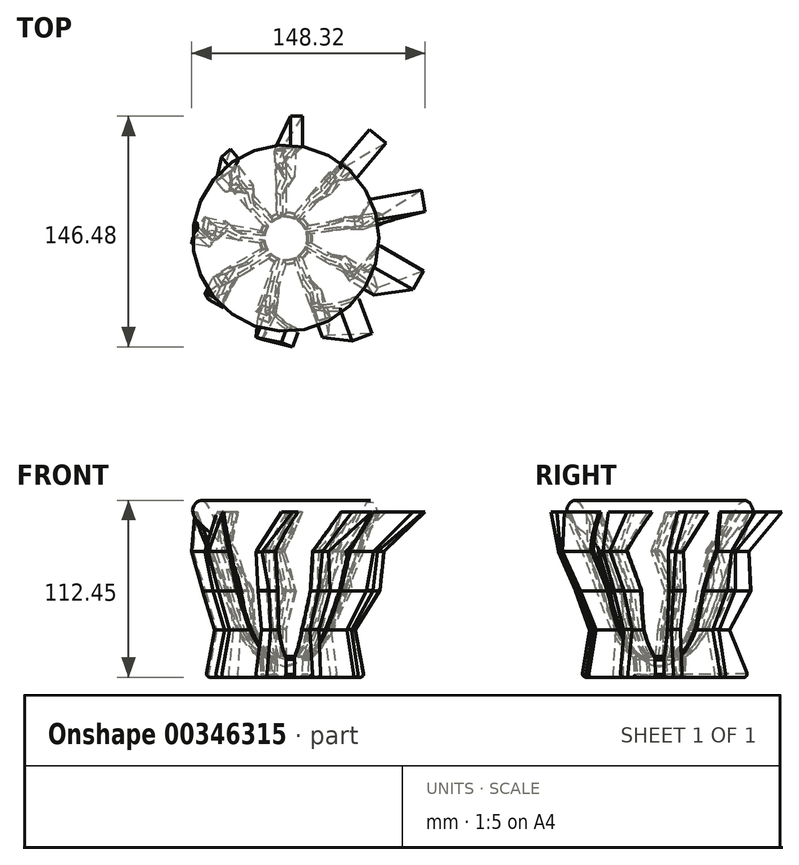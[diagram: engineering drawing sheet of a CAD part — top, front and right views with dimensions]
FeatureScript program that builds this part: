
annotation { "Feature Type Name" : "Feature", "Feature Type Description" : "" }
export const myFeature = defineFeature(function(context is Context, id is Id, definition is map)
    precondition{}
    {
        {
            var Q0;
            Q0=qCreatedBy(makeId("Top.planeOp"),FACE);
            var sketch = newSketch(context, id + "F0", { "sketchPlane" : qUnion([Q0])});
            skLineSegment(sketch, "E0", {"start": v(-7.56, 56.38) * mm, "end": v(0, 56.38) * mm});
            skLineSegment(sketch, "E1", {"start": v(0, 56.38) * mm, "end": v(0, 16) * mm});
            skLineSegment(sketch, "E2.1.1", {"start": v(-36.67, 35.22) * mm, "end": v(-30.87, 40.08) * mm});
            skLineSegment(sketch, "E2.1.2", {"start": v(-30.87, 40.08) * mm, "end": v(-8.58, 13.5) * mm});
            skLineSegment(sketch, "E2.2.1", {"start": v(-50.73, 3.4) * mm, "end": v(-49.41, 10.86) * mm});
            skLineSegment(sketch, "E2.2.2", {"start": v(-49.41, 10.86) * mm, "end": v(-15.25, 4.83) * mm});
            skLineSegment(sketch, "E2.3.1", {"start": v(-41.05, -30) * mm, "end": v(-44.83, -23.44) * mm});
            skLineSegment(sketch, "E2.3.2", {"start": v(-44.83, -23.44) * mm, "end": v(-14.8, -6.1) * mm});
            skLineSegment(sketch, "E2.4.1", {"start": v(-12.17, -49.36) * mm, "end": v(-19.27, -46.78) * mm});
            skLineSegment(sketch, "E2.4.2", {"start": v(-19.27, -46.78) * mm, "end": v(-7.4, -14.18) * mm});
            skLineSegment(sketch, "E2.5.1", {"start": v(22.28, -45.29) * mm, "end": v(17.16, -47.15) * mm});
            skLineSegment(sketch, "E2.5.2", {"start": v(17.16, -47.15) * mm, "end": v(5.47, -15.04) * mm});
            skLineSegment(sketch, "E2.6.1", {"start": v(46.18, -20.37) * mm, "end": v(43.45, -25.09) * mm});
            skLineSegment(sketch, "E2.6.2", {"start": v(43.45, -25.09) * mm, "end": v(13.86, -8) * mm});
            skLineSegment(sketch, "E2.7.1", {"start": v(48.83, 14.15) * mm, "end": v(49.78, 8.78) * mm});
            skLineSegment(sketch, "E2.7.2", {"start": v(49.78, 8.78) * mm, "end": v(15.76, 2.78) * mm});
            skLineSegment(sketch, "E2.8.1", {"start": v(28.32, 42.23) * mm, "end": v(32.5, 38.72) * mm});
            skLineSegment(sketch, "E2.8.2", {"start": v(32.5, 38.72) * mm, "end": v(10.28, 12.26) * mm});
            skPoint(sketch, "E2.center", {"position": v(0, 0) * mm});
            skArc(sketch, "E3", {"start": v(-13.84, 8.02) * mm, "mid": v(-14.64, 6.47) * mm, "end": v(-15.25, 4.83) * mm});
            skArc(sketch, "E4.trimOffspring", {"start": v(-5.45, 15.04) * mm, "mid": v(-7.06, 14.36) * mm, "end": v(-8.58, 13.5) * mm});
            skArc(sketch, "E5.trimOffspring", {"start": v(5.5, 15.03) * mm, "mid": v(2.79, 15.75) * mm, "end": v(0, 16) * mm});
            skLineSegment(sketch, "E6.trimOffspring", {"start": v(-5.45, 15.04) * mm, "end": v(-7.56, 56.38) * mm});
            skLineSegment(sketch, "E7.trimOffspring", {"start": v(15.75, -2.8) * mm, "end": v(46.18, -20.37) * mm});
            skLineSegment(sketch, "E8.trimOffspring", {"start": v(13.87, 7.98) * mm, "end": v(48.83, 14.15) * mm});
            skLineSegment(sketch, "E9.trimOffspring", {"start": v(5.5, 15.03) * mm, "end": v(28.32, 42.23) * mm});
            skLineSegment(sketch, "E10.trimOffspring", {"start": v(-13.84, 8.02) * mm, "end": v(-36.67, 35.22) * mm});
            skLineSegment(sketch, "E11.trimOffspring", {"start": v(-15.76, -2.76) * mm, "end": v(-50.73, 3.4) * mm});
            skArc(sketch, "E12.trimOffspring", {"start": v(-15.76, -2.76) * mm, "mid": v(-15.37, -4.45) * mm, "end": v(-14.8, -6.1) * mm});
            skArc(sketch, "E13.trimOffspring", {"start": v(-10.3, -12.24) * mm, "mid": v(-8.9, -13.3) * mm, "end": v(-7.4, -14.18) * mm});
            skLineSegment(sketch, "E14.trimOffspring", {"start": v(-10.3, -12.24) * mm, "end": v(-41.05, -30) * mm});
            skArc(sketch, "E15.trimOffspring", {"start": v(-0.02, -16) * mm, "mid": v(2.77, -15.76) * mm, "end": v(5.47, -15.04) * mm});
            skLineSegment(sketch, "E16.trimOffspring", {"start": v(-0.02, -16) * mm, "end": v(-12.17, -49.36) * mm});
            skLineSegment(sketch, "E17.trimOffspring", {"start": v(10.27, -12.27) * mm, "end": v(22.28, -45.29) * mm});
            skArc(sketch, "E18.trimOffspring", {"start": v(13.87, 7.98) * mm, "mid": v(12.26, 10.28) * mm, "end": v(10.28, 12.26) * mm});
            skArc(sketch, "E19.trimOffspring", {"start": v(15.75, -2.8) * mm, "mid": v(16, -0.01) * mm, "end": v(15.76, 2.78) * mm});
            skArc(sketch, "E20.trimOffspring", {"start": v(10.27, -12.27) * mm, "mid": v(12.25, -10.3) * mm, "end": v(13.86, -8) * mm});
            skSolve(sketch);
        }
        {
            var Q0;
            Q0=qCreatedBy(makeId("Top.planeOp"),FACE);
            cPlane(context, id + "F1", {"entities" : qUnion([Q0]), "cplaneType" : CPlaneType.OFFSET, "offset" : 30 * mm, "width" : 150 * mm, "height" : 150 * mm});
        }
        {
            var Q0;
            Q0=qCreatedBy(id+"F1.planeOp",FACE);
            cPlane(context, id + "F2", {"entities" : qUnion([Q0]), "cplaneType" : CPlaneType.OFFSET, "offset" : 25 * mm, "width" : 150 * mm, "height" : 150 * mm});
        }
        {
            var Q0;
            Q0=qCreatedBy(id+"F1.planeOp",FACE);
            var sketch = newSketch(context, id + "F3", { "sketchPlane" : qUnion([Q0])});
            skLineSegment(sketch, "E21", {"start": v(-6, 44.23) * mm, "end": v(0, 44.23) * mm});
            skLineSegment(sketch, "E22", {"start": v(0, 44.23) * mm, "end": v(0, 17.12) * mm});
            skLineSegment(sketch, "E23.1.1", {"start": v(-33.34, 29.91) * mm, "end": v(-28.74, 33.77) * mm});
            skLineSegment(sketch, "E23.1.2", {"start": v(-28.74, 33.77) * mm, "end": v(-11.31, 13) * mm});
            skLineSegment(sketch, "E23.2.1", {"start": v(-45.08, 1.36) * mm, "end": v(-44.04, 7.27) * mm});
            skLineSegment(sketch, "E23.2.2", {"start": v(-44.04, 7.27) * mm, "end": v(-17.34, 2.56) * mm});
            skLineSegment(sketch, "E23.3.1", {"start": v(-35.73, -28.05) * mm, "end": v(-38.73, -22.86) * mm});
            skLineSegment(sketch, "E23.3.2", {"start": v(-38.73, -22.86) * mm, "end": v(-15.24, -9.3) * mm});
            skLineSegment(sketch, "E23.4.1", {"start": v(-9.65, -44.58) * mm, "end": v(-15.29, -42.52) * mm});
            skLineSegment(sketch, "E23.4.2", {"start": v(-15.29, -42.52) * mm, "end": v(-6.02, -17.04) * mm});
            skLineSegment(sketch, "E23.5.1", {"start": v(20.94, -40.47) * mm, "end": v(15.3, -42.52) * mm});
            skLineSegment(sketch, "E23.5.2", {"start": v(15.3, -42.52) * mm, "end": v(6.03, -17.04) * mm});
            skLineSegment(sketch, "E23.6.1", {"start": v(41.74, -17.66) * mm, "end": v(38.74, -22.86) * mm});
            skLineSegment(sketch, "E23.6.2", {"start": v(38.74, -22.86) * mm, "end": v(15.26, -9.3) * mm});
            skLineSegment(sketch, "E23.7.1", {"start": v(43.01, 13.18) * mm, "end": v(44.06, 7.27) * mm});
            skLineSegment(sketch, "E23.7.2", {"start": v(44.06, 7.27) * mm, "end": v(17.35, 2.56) * mm});
            skLineSegment(sketch, "E23.8.1", {"start": v(24.16, 37.63) * mm, "end": v(28.76, 33.77) * mm});
            skLineSegment(sketch, "E23.8.2", {"start": v(28.76, 33.77) * mm, "end": v(11.33, 13) * mm});
            skPoint(sketch, "E23.center", {"position": v(0, -0.5) * mm});
            skArc(sketch, "E24", {"start": v(-15.23, 8.33) * mm, "mid": v(-16.54, 5.54) * mm, "end": v(-17.34, 2.56) * mm});
            skArc(sketch, "E25.trimOffspring", {"start": v(-6, 16.07) * mm, "mid": v(-8.79, 14.77) * mm, "end": v(-11.31, 13) * mm});
            skArc(sketch, "E26.trimOffspring", {"start": v(6.06, 16.05) * mm, "mid": v(3.08, 16.85) * mm, "end": v(0, 17.12) * mm});
            skLineSegment(sketch, "E27.trimOffspring", {"start": v(-6, 16.07) * mm, "end": v(-6, 44.23) * mm});
            skLineSegment(sketch, "E28.trimOffspring", {"start": v(17.35, -3.58) * mm, "end": v(41.74, -17.66) * mm});
            skLineSegment(sketch, "E29.trimOffspring", {"start": v(15.27, 8.3) * mm, "end": v(43.01, 13.18) * mm});
            skLineSegment(sketch, "E30.trimOffspring", {"start": v(6.06, 16.05) * mm, "end": v(24.16, 37.63) * mm});
            skLineSegment(sketch, "E31.trimOffspring", {"start": v(-15.23, 8.33) * mm, "end": v(-33.34, 29.91) * mm});
            skLineSegment(sketch, "E32.trimOffspring", {"start": v(-17.34, -3.53) * mm, "end": v(-45.08, 1.36) * mm});
            skArc(sketch, "E33.trimOffspring", {"start": v(-17.34, -3.53) * mm, "mid": v(-16.55, -6.5) * mm, "end": v(-15.24, -9.3) * mm});
            skArc(sketch, "E34.trimOffspring", {"start": v(-11.33, -13.97) * mm, "mid": v(-8.8, -15.74) * mm, "end": v(-6.02, -17.04) * mm});
            skLineSegment(sketch, "E35.trimOffspring", {"start": v(-11.33, -13.97) * mm, "end": v(-35.73, -28.05) * mm});
            skArc(sketch, "E36.trimOffspring", {"start": v(-0.02, -18.1) * mm, "mid": v(3.05, -17.84) * mm, "end": v(6.03, -17.04) * mm});
            skLineSegment(sketch, "E37.trimOffspring", {"start": v(-0.02, -18.1) * mm, "end": v(-9.65, -44.58) * mm});
            skLineSegment(sketch, "E38.trimOffspring", {"start": v(11.31, -14) * mm, "end": v(20.94, -40.47) * mm});
            skArc(sketch, "E39.trimOffspring", {"start": v(15.27, 8.3) * mm, "mid": v(13.5, 10.82) * mm, "end": v(11.33, 13) * mm});
            skArc(sketch, "E40.trimOffspring", {"start": v(17.35, -3.58) * mm, "mid": v(17.62, -0.5) * mm, "end": v(17.35, 2.56) * mm});
            skArc(sketch, "E41.trimOffspring", {"start": v(11.31, -14) * mm, "mid": v(13.5, -11.83) * mm, "end": v(15.26, -9.3) * mm});
            skSolve(sketch);
        }
        {
            var Q0;
            Q0=makeQuery(id+"F3.imprint","IMPRINT",FACE,{"disambiguationData":[TD([[makeQuery(id+"F3.imprint","IMPRINT",EDGE,{"derivedFrom":sQuery(id+"F3.wireOp",EDGE,"E21")}),-1.0]])]});
            var Q1;
            Q1=makeQuery(id+"F0.imprint","IMPRINT",FACE,{"disambiguationData":[TD([[makeQuery(id+"F0.imprint","IMPRINT",EDGE,{"derivedFrom":sQuery(id+"F0.wireOp",EDGE,"E0")}),-1.0]])]});
            loft(context, id + "F4", {"sheetProfilesArray" : [{ "sheetProfileEntities" : qUnion([Q0]) }, { "sheetProfileEntities" : qUnion([Q1]) }]});
        }
        {
            var Q0;
            Q0=qCreatedBy(id+"F2.planeOp",FACE);
            var sketch = newSketch(context, id + "F5", { "sketchPlane" : qUnion([Q0])});
            skLineSegment(sketch, "E42", {"start": v(-1.16, 57.95) * mm, "end": v(6.4, 57.6) * mm});
            skLineSegment(sketch, "E43", {"start": v(6.4, 57.6) * mm, "end": v(4.86, 23.47) * mm});
            skLineSegment(sketch, "E44.1.1", {"start": v(-36.4, 41.47) * mm, "end": v(-30.4, 46.06) * mm});
            skLineSegment(sketch, "E44.1.2", {"start": v(-30.4, 46.06) * mm, "end": v(-9.63, 18.92) * mm});
            skLineSegment(sketch, "E44.2.1", {"start": v(-52.8, 6.18) * mm, "end": v(-51.16, 13.57) * mm});
            skLineSegment(sketch, "E44.2.2", {"start": v(-51.16, 13.57) * mm, "end": v(-17.8, 6.12) * mm});
            skLineSegment(sketch, "E44.3.1", {"start": v(-42.7, -31.39) * mm, "end": v(-46.18, -24.68) * mm});
            skLineSegment(sketch, "E44.3.2", {"start": v(-46.18, -24.68) * mm, "end": v(-15.84, -8.94) * mm});
            skLineSegment(sketch, "E44.4.1", {"start": v(-10.8, -53.67) * mm, "end": v(-17.78, -50.77) * mm});
            skLineSegment(sketch, "E44.4.2", {"start": v(-17.78, -50.77) * mm, "end": v(-4.66, -19.21) * mm});
            skLineSegment(sketch, "E44.5.1", {"start": v(27.96, -50.24) * mm, "end": v(20.74, -52.5) * mm});
            skLineSegment(sketch, "E44.5.2", {"start": v(20.74, -52.5) * mm, "end": v(10.51, -19.9) * mm});
            skLineSegment(sketch, "E44.6.1", {"start": v(55.44, -22.7) * mm, "end": v(51.37, -29.07) * mm});
            skLineSegment(sketch, "E44.6.2", {"start": v(51.37, -29.07) * mm, "end": v(22.57, -10.66) * mm});
            skLineSegment(sketch, "E44.7.1", {"start": v(58.8, 16.07) * mm, "end": v(59.77, 8.57) * mm});
            skLineSegment(sketch, "E44.7.2", {"start": v(59.77, 8.57) * mm, "end": v(25.88, 4.16) * mm});
            skLineSegment(sketch, "E44.8.1", {"start": v(36.44, 47.92) * mm, "end": v(42, 42.8) * mm});
            skLineSegment(sketch, "E44.8.2", {"start": v(42, 42.8) * mm, "end": v(18.88, 17.64) * mm});
            skPoint(sketch, "E44.center", {"position": v(3.86, 1.29) * mm});
            skArc(sketch, "E45", {"start": v(-14.83, 13.27) * mm, "mid": v(-16.63, 9.83) * mm, "end": v(-17.8, 6.12) * mm});
            skArc(sketch, "E46.trimOffspring", {"start": v(-2.75, 22.48) * mm, "mid": v(-6.35, 21) * mm, "end": v(-9.63, 18.92) * mm});
            skArc(sketch, "E47.trimOffspring", {"start": v(12.42, 21.78) * mm, "mid": v(8.71, 22.95) * mm, "end": v(4.86, 23.47) * mm});
            skLineSegment(sketch, "E48.trimOffspring", {"start": v(-2.75, 22.48) * mm, "end": v(-1.16, 57.95) * mm});
            skLineSegment(sketch, "E49.trimOffspring", {"start": v(25.52, -3.58) * mm, "end": v(55.44, -22.7) * mm});
            skLineSegment(sketch, "E50.trimOffspring", {"start": v(23.58, 11.48) * mm, "end": v(58.8, 16.07) * mm});
            skLineSegment(sketch, "E51.trimOffspring", {"start": v(12.42, 21.78) * mm, "end": v(36.44, 47.92) * mm});
            skLineSegment(sketch, "E52.trimOffspring", {"start": v(-14.83, 13.27) * mm, "end": v(-36.4, 41.47) * mm});
            skLineSegment(sketch, "E53.trimOffspring", {"start": v(-18.15, -1.55) * mm, "end": v(-52.8, 6.18) * mm});
            skArc(sketch, "E54.trimOffspring", {"start": v(-18.15, -1.55) * mm, "mid": v(-17.32, -5.34) * mm, "end": v(-15.84, -8.94) * mm});
            skArc(sketch, "E55.trimOffspring", {"start": v(-11.18, -15.04) * mm, "mid": v(-8.1, -17.4) * mm, "end": v(-4.66, -19.21) * mm});
            skLineSegment(sketch, "E56.trimOffspring", {"start": v(-11.18, -15.04) * mm, "end": v(-42.7, -31.39) * mm});
            skArc(sketch, "E57.trimOffspring", {"start": v(2.83, -20.89) * mm, "mid": v(6.72, -20.73) * mm, "end": v(10.51, -19.9) * mm});
            skLineSegment(sketch, "E58.trimOffspring", {"start": v(2.83, -20.89) * mm, "end": v(-10.8, -53.67) * mm});
            skLineSegment(sketch, "E59.trimOffspring", {"start": v(17.33, -16.36) * mm, "end": v(27.96, -50.24) * mm});
            skArc(sketch, "E60.trimOffspring", {"start": v(23.58, 11.48) * mm, "mid": v(21.5, 14.77) * mm, "end": v(18.88, 17.64) * mm});
            skArc(sketch, "E61.trimOffspring", {"start": v(25.52, -3.58) * mm, "mid": v(26.04, 0.27) * mm, "end": v(25.88, 4.16) * mm});
            skArc(sketch, "E62.trimOffspring", {"start": v(17.33, -16.36) * mm, "mid": v(20.2, -13.74) * mm, "end": v(22.57, -10.66) * mm});
            skSolve(sketch);
        }
        {
            var Q0;
            Q0=makeQuery(id+"F5.imprint","IMPRINT",FACE,{"disambiguationData":[TD([[makeQuery(id+"F5.imprint","IMPRINT",EDGE,{"derivedFrom":sQuery(id+"F5.wireOp",EDGE,"E42")}),-1.0]])]});
            var Q1;
            Q1=makeQuery(id+"F3.imprint","IMPRINT",FACE,{"disambiguationData":[TD([[makeQuery(id+"F3.imprint","IMPRINT",EDGE,{"derivedFrom":sQuery(id+"F3.wireOp",EDGE,"E21")}),-1.0]])]});
            loft(context, id + "F6", {"sheetProfilesArray" : [{ "sheetProfileEntities" : qUnion([Q0]) }, { "sheetProfileEntities" : qUnion([Q1]) }]});
        }
        {
            var Q0;
            Q0=qCreatedBy(id+"F2.planeOp",FACE);
            cPlane(context, id + "F7", {"entities" : qUnion([Q0]), "cplaneType" : CPlaneType.OFFSET, "offset" : 25 * mm, "width" : 150 * mm, "height" : 150 * mm});
        }
        {
            var Q0;
            Q0=qCreatedBy(id+"F7.planeOp",FACE);
            var sketch = newSketch(context, id + "F8", { "sketchPlane" : qUnion([Q0])});
            skLineSegment(sketch, "E63", {"start": v(-6.84, 56.67) * mm, "end": v(-2.84, 56.67) * mm});
            skLineSegment(sketch, "E64", {"start": v(-2.84, 56.67) * mm, "end": v(4.38, 27.95) * mm});
            skLineSegment(sketch, "E65.1.1", {"start": v(-44.3, 36.24) * mm, "end": v(-41.23, 38.8) * mm});
            skLineSegment(sketch, "E65.1.2", {"start": v(-41.23, 38.8) * mm, "end": v(-18.45, 19.63) * mm});
            skLineSegment(sketch, "E65.2.1", {"start": v(-59.8, -3.39) * mm, "end": v(-59.11, 0.55) * mm});
            skLineSegment(sketch, "E65.2.2", {"start": v(-59.11, 0.55) * mm, "end": v(-28.6, 0.37) * mm});
            skLineSegment(sketch, "E65.3.1", {"start": v(-49.34, -38.88) * mm, "end": v(-51.34, -35.42) * mm});
            skLineSegment(sketch, "E65.3.2", {"start": v(-51.34, -35.42) * mm, "end": v(-25.84, -17.68) * mm});
            skLineSegment(sketch, "E65.4.1", {"start": v(-15.04, -64.35) * mm, "end": v(-18.8, -62.98) * mm});
            skLineSegment(sketch, "E65.4.2", {"start": v(-18.8, -62.98) * mm, "end": v(-8.23, -33.95) * mm});
            skLineSegment(sketch, "E65.5.1", {"start": v(27.14, -61.7) * mm, "end": v(23.38, -63.07) * mm});
            skLineSegment(sketch, "E65.5.2", {"start": v(23.38, -63.07) * mm, "end": v(12.97, -34.47) * mm});
            skLineSegment(sketch, "E65.6.1", {"start": v(58.35, -31.68) * mm, "end": v(55.85, -36) * mm});
            skLineSegment(sketch, "E65.6.2", {"start": v(55.85, -36) * mm, "end": v(30.13, -21.16) * mm});
            skLineSegment(sketch, "E65.7.1", {"start": v(61.45, 14.9) * mm, "end": v(62.32, 9.97) * mm});
            skLineSegment(sketch, "E65.7.2", {"start": v(62.32, 9.97) * mm, "end": v(34.76, 0.65) * mm});
            skLineSegment(sketch, "E65.8.1", {"start": v(35.04, 48.15) * mm, "end": v(38.1, 45.58) * mm});
            skLineSegment(sketch, "E65.8.2", {"start": v(38.1, 45.58) * mm, "end": v(23.7, 20.46) * mm});
            skPoint(sketch, "E65.center", {"position": v(0.72, 0.29) * mm});
            skArc(sketch, "E66", {"start": v(-24.33, 12.45) * mm, "mid": v(-27.07, 6.62) * mm, "end": v(-28.6, 0.37) * mm});
            skArc(sketch, "E67.trimOffspring", {"start": v(-6.84, 26.39) * mm, "mid": v(-13, 23.62) * mm, "end": v(-18.45, 19.63) * mm});
            skArc(sketch, "E68.trimOffspring", {"start": v(15.88, 25.31) * mm, "mid": v(10.25, 27.16) * mm, "end": v(4.38, 27.95) * mm});
            skLineSegment(sketch, "E69.trimOffspring", {"start": v(-6.84, 26.39) * mm, "end": v(-6.84, 56.67) * mm});
            skLineSegment(sketch, "E70.trimOffspring", {"start": v(33.88, -12.8) * mm, "end": v(58.35, -31.68) * mm});
            skLineSegment(sketch, "E71.trimOffspring", {"start": v(31.38, 10.95) * mm, "end": v(61.45, 14.9) * mm});
            skLineSegment(sketch, "E72.trimOffspring", {"start": v(15.88, 25.31) * mm, "end": v(35.04, 48.15) * mm});
            skLineSegment(sketch, "E73.trimOffspring", {"start": v(-24.33, 12.45) * mm, "end": v(-44.3, 36.24) * mm});
            skLineSegment(sketch, "E74.trimOffspring", {"start": v(-28.52, -8.9) * mm, "end": v(-59.8, -3.39) * mm});
            skArc(sketch, "E75.trimOffspring", {"start": v(-28.52, -8.9) * mm, "mid": v(-27.5, -13.4) * mm, "end": v(-25.84, -17.68) * mm});
            skArc(sketch, "E76.trimOffspring", {"start": v(-18.52, -27.62) * mm, "mid": v(-13.68, -31.27) * mm, "end": v(-8.23, -33.95) * mm});
            skLineSegment(sketch, "E77.trimOffspring", {"start": v(-18.52, -27.62) * mm, "end": v(-49.34, -38.88) * mm});
            skArc(sketch, "E78.trimOffspring", {"start": v(0.75, -35.94) * mm, "mid": v(6.93, -35.8) * mm, "end": v(12.97, -34.47) * mm});
            skLineSegment(sketch, "E79.trimOffspring", {"start": v(0.75, -35.94) * mm, "end": v(-15.04, -64.35) * mm});
            skLineSegment(sketch, "E80.trimOffspring", {"start": v(21.2, -30.42) * mm, "end": v(27.14, -61.7) * mm});
            skArc(sketch, "E81.trimOffspring", {"start": v(31.38, 10.95) * mm, "mid": v(28, 16.08) * mm, "end": v(23.7, 20.46) * mm});
            skArc(sketch, "E82.trimOffspring", {"start": v(33.88, -12.8) * mm, "mid": v(35.03, -6.12) * mm, "end": v(34.76, 0.65) * mm});
            skArc(sketch, "E83.trimOffspring", {"start": v(21.2, -30.42) * mm, "mid": v(26.14, -26.24) * mm, "end": v(30.13, -21.16) * mm});
            skSolve(sketch);
        }
        {
            var Q1;
            Q1=makeQuery(id+"F8.imprint","IMPRINT",FACE,{"disambiguationData":[TD([[makeQuery(id+"F8.imprint","IMPRINT",EDGE,{"derivedFrom":sQuery(id+"F8.wireOp",EDGE,"E63")}),-1.0]])]});
            var Q2;
            Q2=makeQuery(id+"F5.imprint","IMPRINT",FACE,{"disambiguationData":[TD([[makeQuery(id+"F5.imprint","IMPRINT",EDGE,{"derivedFrom":sQuery(id+"F5.wireOp",EDGE,"E42")}),-1.0]])]});
            loft(context, id + "F9", {"operationType" : NewBodyOperationType.ADD, "sheetProfilesArray" : [{ "sheetProfileEntities" : qUnion([Q1]) }, { "sheetProfileEntities" : qUnion([Q2]) }]});
        }
        {
            var Q0;
            Q0=qCreatedBy(id+"F7.planeOp",FACE);
            cPlane(context, id + "F10", {"entities" : qUnion([Q0]), "cplaneType" : CPlaneType.OFFSET, "offset" : 25 * mm, "width" : 150 * mm, "height" : 150 * mm});
        }
        {
            var Q0;
            Q0=qCreatedBy(id+"F10.planeOp",FACE);
            var sketch = newSketch(context, id + "F11", { "sketchPlane" : qUnion([Q0])});
            skLineSegment(sketch, "E84", {"start": v(2.9, 77.48) * mm, "end": v(10.46, 77.48) * mm});
            skLineSegment(sketch, "E85", {"start": v(10.46, 77.48) * mm, "end": v(10.46, 38.6) * mm});
            skLineSegment(sketch, "E86.1.1", {"start": v(-40.91, 51.61) * mm, "end": v(-35.12, 56.48) * mm});
            skLineSegment(sketch, "E86.1.2", {"start": v(-35.12, 56.48) * mm, "end": v(-17.8, 35.83) * mm});
            skLineSegment(sketch, "E86.2.1", {"start": v(-57.85, 3.64) * mm, "end": v(-56.53, 11.1) * mm});
            skLineSegment(sketch, "E86.2.2", {"start": v(-56.53, 11.1) * mm, "end": v(-39.19, 8.03) * mm});
            skLineSegment(sketch, "E86.3.1", {"start": v(-39.98, -44) * mm, "end": v(-43.76, -37.44) * mm});
            skLineSegment(sketch, "E86.3.2", {"start": v(-43.76, -37.44) * mm, "end": v(-28.14, -28.42) * mm});
            skLineSegment(sketch, "E86.4.1", {"start": v(4.32, -69) * mm, "end": v(-2.79, -66.41) * mm});
            skLineSegment(sketch, "E86.4.2", {"start": v(-2.79, -66.41) * mm, "end": v(7.06, -39.37) * mm});
            skLineSegment(sketch, "E86.5.1", {"start": v(54.7, -60.68) * mm, "end": v(41.9, -65.34) * mm});
            skLineSegment(sketch, "E86.5.2", {"start": v(41.9, -65.34) * mm, "end": v(28.37, -28.2) * mm});
            skLineSegment(sketch, "E86.6.1", {"start": v(87.57, -20.92) * mm, "end": v(80.76, -32.72) * mm});
            skLineSegment(sketch, "E86.6.2", {"start": v(80.76, -32.72) * mm, "end": v(39.06, -8.64) * mm});
            skLineSegment(sketch, "E86.7.1", {"start": v(86.16, 30.48) * mm, "end": v(88.52, 17.06) * mm});
            skLineSegment(sketch, "E86.7.2", {"start": v(88.52, 17.06) * mm, "end": v(39.12, 8.35) * mm});
            skLineSegment(sketch, "E86.8.1", {"start": v(53.08, 69.13) * mm, "end": v(63.52, 60.37) * mm});
            skLineSegment(sketch, "E86.8.2", {"start": v(63.52, 60.37) * mm, "end": v(32.47, 23.37) * mm});
            skPoint(sketch, "E86.center", {"position": v(-1.01, 1.3) * mm});
            skArc(sketch, "E87", {"start": v(-24.28, 31.8) * mm, "mid": v(-33.88, 21.26) * mm, "end": v(-39.19, 8.03) * mm});
            skArc(sketch, "E88.trimOffspring", {"start": v(2.9, 39.9) * mm, "mid": v(-7.72, 39.25) * mm, "end": v(-17.8, 35.83) * mm});
            skArc(sketch, "E89.trimOffspring", {"start": v(22.7, 32.93) * mm, "mid": v(16.82, 36.3) * mm, "end": v(10.46, 38.6) * mm});
            skLineSegment(sketch, "E90.trimOffspring", {"start": v(2.9, 39.9) * mm, "end": v(2.9, 77.48) * mm});
            skLineSegment(sketch, "E91.trimOffspring", {"start": v(39.4, 6.9) * mm, "end": v(87.57, -20.92) * mm});
            skLineSegment(sketch, "E92.trimOffspring", {"start": v(33.88, 21.26) * mm, "end": v(86.16, 30.48) * mm});
            skLineSegment(sketch, "E93.trimOffspring", {"start": v(22.7, 32.93) * mm, "end": v(53.08, 69.13) * mm});
            skLineSegment(sketch, "E94.trimOffspring", {"start": v(-24.28, 31.8) * mm, "end": v(-40.91, 51.61) * mm});
            skLineSegment(sketch, "E95.trimOffspring", {"start": v(-40, 0.5) * mm, "end": v(-57.85, 3.64) * mm});
            skArc(sketch, "E96.trimOffspring", {"start": v(-40, 0.5) * mm, "mid": v(-37.01, -15.17) * mm, "end": v(-28.14, -28.42) * mm});
            skArc(sketch, "E97.trimOffspring", {"start": v(-21.84, -33.51) * mm, "mid": v(-7.95, -39.2) * mm, "end": v(7.06, -39.37) * mm});
            skLineSegment(sketch, "E98.trimOffspring", {"start": v(-21.84, -33.51) * mm, "end": v(-39.98, -44) * mm});
            skArc(sketch, "E99.trimOffspring", {"start": v(16.1, -36.61) * mm, "mid": v(22.64, -32.98) * mm, "end": v(28.37, -28.2) * mm});
            skLineSegment(sketch, "E100.trimOffspring", {"start": v(16.1, -36.61) * mm, "end": v(4.32, -69) * mm});
            skLineSegment(sketch, "E101.trimOffspring", {"start": v(37.59, -13.68) * mm, "end": v(54.7, -60.68) * mm});
            skArc(sketch, "E102.trimOffspring", {"start": v(33.88, 21.26) * mm, "mid": v(33.19, 22.33) * mm, "end": v(32.47, 23.37) * mm});
            skArc(sketch, "E103.trimOffspring", {"start": v(39.4, 6.9) * mm, "mid": v(39.27, 7.62) * mm, "end": v(39.12, 8.35) * mm});
            skArc(sketch, "E104.trimOffspring", {"start": v(37.59, -13.68) * mm, "mid": v(38.4, -11.18) * mm, "end": v(39.06, -8.64) * mm});
            skSolve(sketch);
        }
        {
            var Q0;
            Q0=makeQuery(id+"F11.imprint","IMPRINT",FACE,{"disambiguationData":[TD([[makeQuery(id+"F11.imprint","IMPRINT",EDGE,{"derivedFrom":sQuery(id+"F11.wireOp",EDGE,"E84")}),-1.0]])]});
            var Q1;
            Q1=makeQuery(id+"F9.opLoft","CAP_FACE",FACE,{"disambiguationData":[OSD([makeQuery(id+"F8.imprint","IMPRINT",FACE,{"disambiguationData":[TD([[makeQuery(id+"F8.imprint","IMPRINT",EDGE,{"derivedFrom":sQuery(id+"F8.wireOp",EDGE,"E63")}),-1.0]])]})])],"isStart":true});
            loft(context, id + "F12", {"sheetProfilesArray" : [{ "sheetProfileEntities" : qUnion([Q0]) }, { "sheetProfileEntities" : qUnion([Q1]) }]});
        }
        {
            var Q0;
            Q0=qCreatedBy(makeId("Front.planeOp"),FACE);
            var sketch = newSketch(context, id + "F13", { "sketchPlane" : qUnion([Q0])});
            skFitSpline(sketch, "E105", {"points": [v(0, 6.67) * mm, v(22.68, 21.5) * mm, v(41.53, 65.98) * mm, v(66.57, 126.67) * mm, v(67.46, 128.14) * mm], "startDerivative": vector(107.24, 30.8) * mm, "endDerivative": vector(9.87, 13.28) * mm});
            skLineSegment(sketch, "E106", {"start": v(0, 6.67) * mm, "end": v(0, 126.67) * mm});
            skLineSegment(sketch, "E107", {"start": v(0, 126.67) * mm, "end": v(67.46, 128.14) * mm});
            skSolve(sketch);
        }
        {
            var Q0;
            Q0=makeQuery(id+"F13.imprint","IMPRINT",FACE,{"disambiguationData":[TD([[makeQuery(id+"F13.imprint","IMPRINT",EDGE,{"derivedFrom":sQuery(id+"F13.wireOp",EDGE,"E105")}),1.0]])]});
            var Q1;
            Q1=sQuery(id+"F13.wireOp",EDGE,"E106");
            revolve(context, id + "F14", {"operationType" : NewBodyOperationType.REMOVE, "entities" : qUnion([Q0]), "axis" : qUnion([Q1]), "revolveType" : RevolveType.FULL, "oppositeDirection" : true});
        }
        {
            var Q0;
            Q0=makeQuery(id+"F4.opLoft","SWEPT_BODY",BODY,{"disambiguationData":[OSD([makeQuery(id+"F0.imprint","IMPRINT",FACE,{"disambiguationData":[TD([[makeQuery(id+"F0.imprint","IMPRINT",EDGE,{"derivedFrom":sQuery(id+"F0.wireOp",EDGE,"E0")}),-1.0]])]}),makeQuery(id+"F3.imprint","IMPRINT",FACE,{"disambiguationData":[TD([[makeQuery(id+"F3.imprint","IMPRINT",EDGE,{"derivedFrom":sQuery(id+"F3.wireOp",EDGE,"E21")}),-1.0]])]})])]});
            var Q1;
            Q1=makeQuery(id+"F14.boolean.opBoolean","SPLIT",BODY,{"disambiguationData":[OD(0.0)],"derivedFrom":makeQuery(id+"F6.opLoft","SWEPT_BODY",BODY,{"disambiguationData":[OSD([makeQuery(id+"F3.imprint","IMPRINT",FACE,{"disambiguationData":[TD([[makeQuery(id+"F3.imprint","IMPRINT",EDGE,{"derivedFrom":sQuery(id+"F3.wireOp",EDGE,"E21")}),-1.0]])]}),makeQuery(id+"F5.imprint","IMPRINT",FACE,{"disambiguationData":[TD([[makeQuery(id+"F5.imprint","IMPRINT",EDGE,{"derivedFrom":sQuery(id+"F5.wireOp",EDGE,"E42")}),-1.0]])]})])]})});
            var Q2;
            Q2=makeQuery(id+"F14.boolean.opBoolean","SPLIT",BODY,{"disambiguationData":[OD(1.0)],"derivedFrom":makeQuery(id+"F6.opLoft","SWEPT_BODY",BODY,{"disambiguationData":[OSD([makeQuery(id+"F3.imprint","IMPRINT",FACE,{"disambiguationData":[TD([[makeQuery(id+"F3.imprint","IMPRINT",EDGE,{"derivedFrom":sQuery(id+"F3.wireOp",EDGE,"E21")}),-1.0]])]}),makeQuery(id+"F5.imprint","IMPRINT",FACE,{"disambiguationData":[TD([[makeQuery(id+"F5.imprint","IMPRINT",EDGE,{"derivedFrom":sQuery(id+"F5.wireOp",EDGE,"E42")}),-1.0]])]})])]})});
            var Q3;
            Q3=makeQuery(id+"F14.boolean.opBoolean","SPLIT",BODY,{"disambiguationData":[OD(2.0)],"derivedFrom":makeQuery(id+"F6.opLoft","SWEPT_BODY",BODY,{"disambiguationData":[OSD([makeQuery(id+"F3.imprint","IMPRINT",FACE,{"disambiguationData":[TD([[makeQuery(id+"F3.imprint","IMPRINT",EDGE,{"derivedFrom":sQuery(id+"F3.wireOp",EDGE,"E21")}),-1.0]])]}),makeQuery(id+"F5.imprint","IMPRINT",FACE,{"disambiguationData":[TD([[makeQuery(id+"F5.imprint","IMPRINT",EDGE,{"derivedFrom":sQuery(id+"F5.wireOp",EDGE,"E42")}),-1.0]])]})])]})});
            var Q4;
            Q4=makeQuery(id+"F14.boolean.opBoolean","SPLIT",BODY,{"disambiguationData":[OD(3.0)],"derivedFrom":makeQuery(id+"F6.opLoft","SWEPT_BODY",BODY,{"disambiguationData":[OSD([makeQuery(id+"F3.imprint","IMPRINT",FACE,{"disambiguationData":[TD([[makeQuery(id+"F3.imprint","IMPRINT",EDGE,{"derivedFrom":sQuery(id+"F3.wireOp",EDGE,"E21")}),-1.0]])]}),makeQuery(id+"F5.imprint","IMPRINT",FACE,{"disambiguationData":[TD([[makeQuery(id+"F5.imprint","IMPRINT",EDGE,{"derivedFrom":sQuery(id+"F5.wireOp",EDGE,"E42")}),-1.0]])]})])]})});
            var Q5;
            Q5=makeQuery(id+"F14.boolean.opBoolean","SPLIT",BODY,{"disambiguationData":[OD(4.0)],"derivedFrom":makeQuery(id+"F6.opLoft","SWEPT_BODY",BODY,{"disambiguationData":[OSD([makeQuery(id+"F3.imprint","IMPRINT",FACE,{"disambiguationData":[TD([[makeQuery(id+"F3.imprint","IMPRINT",EDGE,{"derivedFrom":sQuery(id+"F3.wireOp",EDGE,"E21")}),-1.0]])]}),makeQuery(id+"F5.imprint","IMPRINT",FACE,{"disambiguationData":[TD([[makeQuery(id+"F5.imprint","IMPRINT",EDGE,{"derivedFrom":sQuery(id+"F5.wireOp",EDGE,"E42")}),-1.0]])]})])]})});
            var Q6;
            Q6=makeQuery(id+"F14.boolean.opBoolean","SPLIT",BODY,{"disambiguationData":[OD(5.0)],"derivedFrom":makeQuery(id+"F6.opLoft","SWEPT_BODY",BODY,{"disambiguationData":[OSD([makeQuery(id+"F3.imprint","IMPRINT",FACE,{"disambiguationData":[TD([[makeQuery(id+"F3.imprint","IMPRINT",EDGE,{"derivedFrom":sQuery(id+"F3.wireOp",EDGE,"E21")}),-1.0]])]}),makeQuery(id+"F5.imprint","IMPRINT",FACE,{"disambiguationData":[TD([[makeQuery(id+"F5.imprint","IMPRINT",EDGE,{"derivedFrom":sQuery(id+"F5.wireOp",EDGE,"E42")}),-1.0]])]})])]})});
            var Q7;
            Q7=makeQuery(id+"F14.boolean.opBoolean","SPLIT",BODY,{"disambiguationData":[OD(6.0)],"derivedFrom":makeQuery(id+"F6.opLoft","SWEPT_BODY",BODY,{"disambiguationData":[OSD([makeQuery(id+"F3.imprint","IMPRINT",FACE,{"disambiguationData":[TD([[makeQuery(id+"F3.imprint","IMPRINT",EDGE,{"derivedFrom":sQuery(id+"F3.wireOp",EDGE,"E21")}),-1.0]])]}),makeQuery(id+"F5.imprint","IMPRINT",FACE,{"disambiguationData":[TD([[makeQuery(id+"F5.imprint","IMPRINT",EDGE,{"derivedFrom":sQuery(id+"F5.wireOp",EDGE,"E42")}),-1.0]])]})])]})});
            var Q8;
            Q8=makeQuery(id+"F14.boolean.opBoolean","SPLIT",BODY,{"disambiguationData":[OD(7.0)],"derivedFrom":makeQuery(id+"F6.opLoft","SWEPT_BODY",BODY,{"disambiguationData":[OSD([makeQuery(id+"F3.imprint","IMPRINT",FACE,{"disambiguationData":[TD([[makeQuery(id+"F3.imprint","IMPRINT",EDGE,{"derivedFrom":sQuery(id+"F3.wireOp",EDGE,"E21")}),-1.0]])]}),makeQuery(id+"F5.imprint","IMPRINT",FACE,{"disambiguationData":[TD([[makeQuery(id+"F5.imprint","IMPRINT",EDGE,{"derivedFrom":sQuery(id+"F5.wireOp",EDGE,"E42")}),-1.0]])]})])]})});
            var Q9;
            Q9=makeQuery(id+"F14.boolean.opBoolean","SPLIT",BODY,{"disambiguationData":[OD(8.0)],"derivedFrom":makeQuery(id+"F6.opLoft","SWEPT_BODY",BODY,{"disambiguationData":[OSD([makeQuery(id+"F3.imprint","IMPRINT",FACE,{"disambiguationData":[TD([[makeQuery(id+"F3.imprint","IMPRINT",EDGE,{"derivedFrom":sQuery(id+"F3.wireOp",EDGE,"E21")}),-1.0]])]}),makeQuery(id+"F5.imprint","IMPRINT",FACE,{"disambiguationData":[TD([[makeQuery(id+"F5.imprint","IMPRINT",EDGE,{"derivedFrom":sQuery(id+"F5.wireOp",EDGE,"E42")}),-1.0]])]})])]})});
            var Q10;
            Q10=makeQuery(id+"F14.boolean.opBoolean","SPLIT",BODY,{"disambiguationData":[OD(0.0)],"derivedFrom":makeQuery(id+"F12.opLoft","SWEPT_BODY",BODY,{"disambiguationData":[OSD([makeQuery(id+"F8.imprint","IMPRINT",FACE,{"disambiguationData":[TD([[makeQuery(id+"F8.imprint","IMPRINT",EDGE,{"derivedFrom":sQuery(id+"F8.wireOp",EDGE,"E63")}),-1.0]])]}),makeQuery(id+"F11.imprint","IMPRINT",FACE,{"disambiguationData":[TD([[makeQuery(id+"F11.imprint","IMPRINT",EDGE,{"derivedFrom":sQuery(id+"F11.wireOp",EDGE,"E84")}),-1.0]])]})])]})});
            var Q11;
            Q11=makeQuery(id+"F14.boolean.opBoolean","SPLIT",BODY,{"disambiguationData":[OD(1.0)],"derivedFrom":makeQuery(id+"F12.opLoft","SWEPT_BODY",BODY,{"disambiguationData":[OSD([makeQuery(id+"F8.imprint","IMPRINT",FACE,{"disambiguationData":[TD([[makeQuery(id+"F8.imprint","IMPRINT",EDGE,{"derivedFrom":sQuery(id+"F8.wireOp",EDGE,"E63")}),-1.0]])]}),makeQuery(id+"F11.imprint","IMPRINT",FACE,{"disambiguationData":[TD([[makeQuery(id+"F11.imprint","IMPRINT",EDGE,{"derivedFrom":sQuery(id+"F11.wireOp",EDGE,"E84")}),-1.0]])]})])]})});
            var Q12;
            Q12=makeQuery(id+"F14.boolean.opBoolean","SPLIT",BODY,{"disambiguationData":[OD(2.0)],"derivedFrom":makeQuery(id+"F12.opLoft","SWEPT_BODY",BODY,{"disambiguationData":[OSD([makeQuery(id+"F8.imprint","IMPRINT",FACE,{"disambiguationData":[TD([[makeQuery(id+"F8.imprint","IMPRINT",EDGE,{"derivedFrom":sQuery(id+"F8.wireOp",EDGE,"E63")}),-1.0]])]}),makeQuery(id+"F11.imprint","IMPRINT",FACE,{"disambiguationData":[TD([[makeQuery(id+"F11.imprint","IMPRINT",EDGE,{"derivedFrom":sQuery(id+"F11.wireOp",EDGE,"E84")}),-1.0]])]})])]})});
            var Q13;
            Q13=makeQuery(id+"F14.boolean.opBoolean","SPLIT",BODY,{"disambiguationData":[OD(3.0)],"derivedFrom":makeQuery(id+"F12.opLoft","SWEPT_BODY",BODY,{"disambiguationData":[OSD([makeQuery(id+"F8.imprint","IMPRINT",FACE,{"disambiguationData":[TD([[makeQuery(id+"F8.imprint","IMPRINT",EDGE,{"derivedFrom":sQuery(id+"F8.wireOp",EDGE,"E63")}),-1.0]])]}),makeQuery(id+"F11.imprint","IMPRINT",FACE,{"disambiguationData":[TD([[makeQuery(id+"F11.imprint","IMPRINT",EDGE,{"derivedFrom":sQuery(id+"F11.wireOp",EDGE,"E84")}),-1.0]])]})])]})});
            var Q14;
            Q14=makeQuery(id+"F14.boolean.opBoolean","SPLIT",BODY,{"disambiguationData":[OD(4.0)],"derivedFrom":makeQuery(id+"F12.opLoft","SWEPT_BODY",BODY,{"disambiguationData":[OSD([makeQuery(id+"F8.imprint","IMPRINT",FACE,{"disambiguationData":[TD([[makeQuery(id+"F8.imprint","IMPRINT",EDGE,{"derivedFrom":sQuery(id+"F8.wireOp",EDGE,"E63")}),-1.0]])]}),makeQuery(id+"F11.imprint","IMPRINT",FACE,{"disambiguationData":[TD([[makeQuery(id+"F11.imprint","IMPRINT",EDGE,{"derivedFrom":sQuery(id+"F11.wireOp",EDGE,"E84")}),-1.0]])]})])]})});
            var Q15;
            Q15=makeQuery(id+"F14.boolean.opBoolean","SPLIT",BODY,{"disambiguationData":[OD(5.0)],"derivedFrom":makeQuery(id+"F12.opLoft","SWEPT_BODY",BODY,{"disambiguationData":[OSD([makeQuery(id+"F8.imprint","IMPRINT",FACE,{"disambiguationData":[TD([[makeQuery(id+"F8.imprint","IMPRINT",EDGE,{"derivedFrom":sQuery(id+"F8.wireOp",EDGE,"E63")}),-1.0]])]}),makeQuery(id+"F11.imprint","IMPRINT",FACE,{"disambiguationData":[TD([[makeQuery(id+"F11.imprint","IMPRINT",EDGE,{"derivedFrom":sQuery(id+"F11.wireOp",EDGE,"E84")}),-1.0]])]})])]})});
            var Q16;
            Q16=makeQuery(id+"F14.boolean.opBoolean","SPLIT",BODY,{"disambiguationData":[OD(6.0)],"derivedFrom":makeQuery(id+"F12.opLoft","SWEPT_BODY",BODY,{"disambiguationData":[OSD([makeQuery(id+"F8.imprint","IMPRINT",FACE,{"disambiguationData":[TD([[makeQuery(id+"F8.imprint","IMPRINT",EDGE,{"derivedFrom":sQuery(id+"F8.wireOp",EDGE,"E63")}),-1.0]])]}),makeQuery(id+"F11.imprint","IMPRINT",FACE,{"disambiguationData":[TD([[makeQuery(id+"F11.imprint","IMPRINT",EDGE,{"derivedFrom":sQuery(id+"F11.wireOp",EDGE,"E84")}),-1.0]])]})])]})});
            var Q17;
            Q17=makeQuery(id+"F14.boolean.opBoolean","SPLIT",BODY,{"disambiguationData":[OD(7.0)],"derivedFrom":makeQuery(id+"F12.opLoft","SWEPT_BODY",BODY,{"disambiguationData":[OSD([makeQuery(id+"F8.imprint","IMPRINT",FACE,{"disambiguationData":[TD([[makeQuery(id+"F8.imprint","IMPRINT",EDGE,{"derivedFrom":sQuery(id+"F8.wireOp",EDGE,"E63")}),-1.0]])]}),makeQuery(id+"F11.imprint","IMPRINT",FACE,{"disambiguationData":[TD([[makeQuery(id+"F11.imprint","IMPRINT",EDGE,{"derivedFrom":sQuery(id+"F11.wireOp",EDGE,"E84")}),-1.0]])]})])]})});
            var Q18;
            Q18=makeQuery(id+"F14.boolean.opBoolean","SPLIT",BODY,{"disambiguationData":[OD(8.0)],"derivedFrom":makeQuery(id+"F12.opLoft","SWEPT_BODY",BODY,{"disambiguationData":[OSD([makeQuery(id+"F8.imprint","IMPRINT",FACE,{"disambiguationData":[TD([[makeQuery(id+"F8.imprint","IMPRINT",EDGE,{"derivedFrom":sQuery(id+"F8.wireOp",EDGE,"E63")}),-1.0]])]}),makeQuery(id+"F11.imprint","IMPRINT",FACE,{"disambiguationData":[TD([[makeQuery(id+"F11.imprint","IMPRINT",EDGE,{"derivedFrom":sQuery(id+"F11.wireOp",EDGE,"E84")}),-1.0]])]})])]})});
            booleanBodies(context, id + "F15", {"operationType" : BooleanOperationType.UNION, "tools" : qUnion([Q0, Q1, Q2, Q3, Q4, Q5, Q6, Q7, Q8, Q9, Q10, Q11, Q12, Q13, Q14, Q15, Q16, Q17, Q18])});
        }
        {
            var Q0;
            Q0=makeQuery(id+"F4.opLoft","CAP_FACE",FACE,{"disambiguationData":[OSD([makeQuery(id+"F0.imprint","IMPRINT",FACE,{"disambiguationData":[TD([[makeQuery(id+"F0.imprint","IMPRINT",EDGE,{"derivedFrom":sQuery(id+"F0.wireOp",EDGE,"E0")}),-1.0]])]})])],"isStart":true});
            var Q1;
            {var subQ0=sQuery(id+"F3.wireOp",EDGE,"E41.trimOffspring");var subQ1=sQuery(id+"F3.wireOp",EDGE,"E38.trimOffspring");var subQ6=sQuery(id+"F3.wireOp",EDGE,"E37.trimOffspring");var subQ7=sQuery(id+"F3.wireOp",EDGE,"E36.trimOffspring");var subQ12=sQuery(id+"F3.wireOp",EDGE,"E23.5.1");var subQ14=sQuery(id+"F3.wireOp",EDGE,"E35.trimOffspring");var subQ15=sQuery(id+"F3.wireOp",EDGE,"E34.trimOffspring");var subQ20=sQuery(id+"F3.wireOp",EDGE,"E23.4.1");var subQ22=sQuery(id+"F3.wireOp",EDGE,"E33.trimOffspring");var subQ23=sQuery(id+"F3.wireOp",EDGE,"E32.trimOffspring");var subQ28=sQuery(id+"F3.wireOp",EDGE,"E23.3.1");var subQ30=sQuery(id+"F3.wireOp",EDGE,"E31.trimOffspring");var subQ31=sQuery(id+"F3.wireOp",EDGE,"E24");var subQ32=sQuery(id+"F3.wireOp",EDGE,"E23.1.1");var subQ36=sQuery(id+"F3.wireOp",EDGE,"E23.6.1");var subQ38=sQuery(id+"F3.wireOp",EDGE,"E30.trimOffspring");var subQ39=sQuery(id+"F3.wireOp",EDGE,"E26.trimOffspring");var subQ44=sQuery(id+"F3.wireOp",EDGE,"E40.trimOffspring");var subQ45=sQuery(id+"F3.wireOp",EDGE,"E28.trimOffspring");var subQ48=sQuery(id+"F3.wireOp",EDGE,"E21");var subQ49=sQuery(id+"F0.wireOp",EDGE,"E0");var subQ50=sQuery(id+"F3.wireOp",EDGE,"E27.trimOffspring");var subQ51=sQuery(id+"F3.wireOp",EDGE,"E25.trimOffspring");var subQ52=sQuery(id+"F0.wireOp",EDGE,"E6.trimOffspring");var subQ53=sQuery(id+"F0.wireOp",EDGE,"E4.trimOffspring");var subQ54=sQuery(id+"F3.wireOp",EDGE,"E39.trimOffspring");var subQ55=sQuery(id+"F3.wireOp",EDGE,"E29.trimOffspring");var subQ56=sQuery(id+"F3.wireOp",EDGE,"E23.7.1");var subQ62=sQuery(id+"F3.wireOp",EDGE,"E23.2.1");var subQ68=sQuery(id+"F3.wireOp",EDGE,"E23.8.1");var subQ73=makeQuery(id+"F14.opRevolve","SWEPT_FACE",FACE,{"disambiguationData":[OSD([sQuery(id+"F13.wireOp",EDGE,"E105")])]});var subQ74=sQuery(id+"F8.wireOp",EDGE,"E72.trimOffspring");var subQ75=sQuery(id+"F8.wireOp",EDGE,"E68.trimOffspring");var subQ76=sQuery(id+"F8.wireOp",EDGE,"E65.8.1");var subQ77=sQuery(id+"F5.wireOp",EDGE,"E51.trimOffspring");var subQ78=sQuery(id+"F5.wireOp",EDGE,"E47.trimOffspring");var subQ79=sQuery(id+"F5.wireOp",EDGE,"E44.8.1");var subQ81=sQuery(id+"F5.wireOp",EDGE,"E60.trimOffspring");var subQ83=sQuery(id+"F8.wireOp",EDGE,"E81.trimOffspring");var subQ85=sQuery(id+"F8.wireOp",EDGE,"E69.trimOffspring");var subQ86=sQuery(id+"F8.wireOp",EDGE,"E67.trimOffspring");var subQ87=sQuery(id+"F8.wireOp",EDGE,"E66");var subQ89=sQuery(id+"F8.wireOp",EDGE,"E65.7.1");var subQ91=sQuery(id+"F8.wireOp",EDGE,"E65.6.1");var subQ93=sQuery(id+"F8.wireOp",EDGE,"E65.5.1");var subQ95=sQuery(id+"F8.wireOp",EDGE,"E65.1.1");var subQ97=sQuery(id+"F8.wireOp",EDGE,"E63");var subQ98=sQuery(id+"F8.wireOp",EDGE,"E65.2.1");var subQ100=sQuery(id+"F8.wireOp",EDGE,"E65.3.1");var subQ102=sQuery(id+"F8.wireOp",EDGE,"E65.4.1");var subQ104=sQuery(id+"F8.wireOp",EDGE,"E70.trimOffspring");var subQ105=sQuery(id+"F8.wireOp",EDGE,"E71.trimOffspring");var subQ106=sQuery(id+"F8.wireOp",EDGE,"E73.trimOffspring");var subQ107=sQuery(id+"F8.wireOp",EDGE,"E74.trimOffspring");var subQ108=sQuery(id+"F8.wireOp",EDGE,"E75.trimOffspring");var subQ109=sQuery(id+"F8.wireOp",EDGE,"E76.trimOffspring");var subQ110=sQuery(id+"F8.wireOp",EDGE,"E77.trimOffspring");var subQ111=sQuery(id+"F8.wireOp",EDGE,"E78.trimOffspring");var subQ112=sQuery(id+"F8.wireOp",EDGE,"E79.trimOffspring");var subQ113=sQuery(id+"F8.wireOp",EDGE,"E80.trimOffspring");var subQ114=sQuery(id+"F8.wireOp",EDGE,"E82.trimOffspring");var subQ115=sQuery(id+"F8.wireOp",EDGE,"E83.trimOffspring");var subQ118=sQuery(id+"F5.wireOp",EDGE,"E50.trimOffspring");var subQ119=sQuery(id+"F5.wireOp",EDGE,"E44.7.1");var subQ120=sQuery(id+"F5.wireOp",EDGE,"E61.trimOffspring");var subQ122=sQuery(id+"F5.wireOp",EDGE,"E49.trimOffspring");var subQ123=sQuery(id+"F5.wireOp",EDGE,"E44.6.1");var subQ124=sQuery(id+"F5.wireOp",EDGE,"E62.trimOffspring");var subQ126=sQuery(id+"F5.wireOp",EDGE,"E59.trimOffspring");var subQ127=sQuery(id+"F5.wireOp",EDGE,"E44.5.1");var subQ128=sQuery(id+"F5.wireOp",EDGE,"E57.trimOffspring");var subQ130=sQuery(id+"F5.wireOp",EDGE,"E58.trimOffspring");var subQ131=sQuery(id+"F5.wireOp",EDGE,"E44.4.1");var subQ132=sQuery(id+"F5.wireOp",EDGE,"E55.trimOffspring");var subQ134=sQuery(id+"F5.wireOp",EDGE,"E56.trimOffspring");var subQ135=sQuery(id+"F5.wireOp",EDGE,"E44.3.1");var subQ136=sQuery(id+"F5.wireOp",EDGE,"E54.trimOffspring");var subQ138=sQuery(id+"F5.wireOp",EDGE,"E53.trimOffspring");var subQ139=sQuery(id+"F5.wireOp",EDGE,"E44.2.1");var subQ140=sQuery(id+"F5.wireOp",EDGE,"E45");var subQ142=sQuery(id+"F5.wireOp",EDGE,"E52.trimOffspring");var subQ143=sQuery(id+"F5.wireOp",EDGE,"E44.1.1");var subQ144=sQuery(id+"F5.wireOp",EDGE,"E46.trimOffspring");var subQ146=sQuery(id+"F5.wireOp",EDGE,"E48.trimOffspring");var subQ147=sQuery(id+"F5.wireOp",EDGE,"E42");var subQ149=sQuery(id+"F11.wireOp",EDGE,"E93.trimOffspring");var subQ150=sQuery(id+"F11.wireOp",EDGE,"E89.trimOffspring");var subQ151=sQuery(id+"F11.wireOp",EDGE,"E86.8.1");var subQ152=sQuery(id+"F11.wireOp",EDGE,"E102.trimOffspring");var subQ155=sQuery(id+"F11.wireOp",EDGE,"E90.trimOffspring");var subQ156=sQuery(id+"F11.wireOp",EDGE,"E88.trimOffspring");var subQ157=sQuery(id+"F11.wireOp",EDGE,"E87");var subQ159=sQuery(id+"F11.wireOp",EDGE,"E86.7.1");var subQ161=sQuery(id+"F11.wireOp",EDGE,"E86.6.1");var subQ163=sQuery(id+"F11.wireOp",EDGE,"E86.5.1");var subQ165=sQuery(id+"F11.wireOp",EDGE,"E86.1.1");var subQ167=sQuery(id+"F11.wireOp",EDGE,"E84");var subQ168=sQuery(id+"F11.wireOp",EDGE,"E86.2.1");var subQ170=sQuery(id+"F11.wireOp",EDGE,"E86.3.1");var subQ172=sQuery(id+"F11.wireOp",EDGE,"E86.4.1");var subQ174=sQuery(id+"F11.wireOp",EDGE,"E91.trimOffspring");var subQ175=sQuery(id+"F11.wireOp",EDGE,"E92.trimOffspring");var subQ176=sQuery(id+"F11.wireOp",EDGE,"E94.trimOffspring");var subQ177=sQuery(id+"F11.wireOp",EDGE,"E95.trimOffspring");var subQ178=sQuery(id+"F11.wireOp",EDGE,"E96.trimOffspring");var subQ179=sQuery(id+"F11.wireOp",EDGE,"E97.trimOffspring");var subQ180=sQuery(id+"F11.wireOp",EDGE,"E98.trimOffspring");var subQ181=sQuery(id+"F11.wireOp",EDGE,"E99.trimOffspring");var subQ182=sQuery(id+"F11.wireOp",EDGE,"E100.trimOffspring");var subQ183=sQuery(id+"F11.wireOp",EDGE,"E101.trimOffspring");var subQ184=sQuery(id+"F11.wireOp",EDGE,"E103.trimOffspring");var subQ185=sQuery(id+"F11.wireOp",EDGE,"E104.trimOffspring");Q1=makeQuery(id+"F15.opBoolean","MERGE",FACE,{"derivedFrom":[makeQuery(id+"F14.boolean.opBoolean","COPY",FACE,{"disambiguationData":[TD([makeQuery(id+"F12.opLoft","SWEPT_FACE",FACE,{"disambiguationData":[OSD([subQ97,subQ86,subQ85,subQ167,subQ156,subQ155])]})])],"derivedFrom":subQ73}),makeQuery(id+"F14.boolean.opBoolean","COPY",FACE,{"disambiguationData":[TD([makeQuery(id+"F12.opLoft","SWEPT_FACE",FACE,{"disambiguationData":[OSD([subQ95,subQ87,subQ106,subQ165,subQ157,subQ176])]})])],"derivedFrom":subQ73}),makeQuery(id+"F14.boolean.opBoolean","COPY",FACE,{"disambiguationData":[TD([makeQuery(id+"F12.opLoft","SWEPT_FACE",FACE,{"disambiguationData":[OSD([subQ98,subQ107,subQ108,subQ168,subQ177,subQ178])]})])],"derivedFrom":subQ73}),makeQuery(id+"F14.boolean.opBoolean","COPY",FACE,{"disambiguationData":[TD([makeQuery(id+"F12.opLoft","SWEPT_FACE",FACE,{"disambiguationData":[OSD([subQ100,subQ109,subQ110,subQ170,subQ179,subQ180])]})])],"derivedFrom":subQ73}),makeQuery(id+"F14.boolean.opBoolean","COPY",FACE,{"disambiguationData":[TD([makeQuery(id+"F12.opLoft","SWEPT_FACE",FACE,{"disambiguationData":[OSD([subQ102,subQ111,subQ112,subQ172,subQ181,subQ182])]})])],"derivedFrom":subQ73}),makeQuery(id+"F14.boolean.opBoolean","COPY",FACE,{"disambiguationData":[TD([makeQuery(id+"F12.opLoft","SWEPT_FACE",FACE,{"disambiguationData":[OSD([subQ93,subQ113,subQ115,subQ163,subQ183,subQ185])]})])],"derivedFrom":subQ73}),makeQuery(id+"F14.boolean.opBoolean","COPY",FACE,{"disambiguationData":[TD([makeQuery(id+"F12.opLoft","SWEPT_FACE",FACE,{"disambiguationData":[OSD([subQ91,subQ104,subQ114,subQ161,subQ174,subQ184])]})])],"derivedFrom":subQ73}),makeQuery(id+"F14.boolean.opBoolean","COPY",FACE,{"disambiguationData":[TD([makeQuery(id+"F12.opLoft","SWEPT_FACE",FACE,{"disambiguationData":[OSD([subQ89,subQ105,subQ83,subQ159,subQ175,subQ152])]})])],"derivedFrom":subQ73}),makeQuery(id+"F14.boolean.opBoolean","COPY",FACE,{"disambiguationData":[TD([makeQuery(id+"F12.opLoft","SWEPT_FACE",FACE,{"disambiguationData":[OSD([subQ76,subQ75,subQ74,subQ151,subQ150,subQ149])]})])],"derivedFrom":subQ73}),makeQuery(id+"F14.boolean.opBoolean","COPY",FACE,{"disambiguationData":[TD([makeQuery(id+"F6.opLoft","SWEPT_FACE",FACE,{"disambiguationData":[OSD([subQ48,subQ51,subQ50,subQ147,subQ144,subQ146])]})])],"derivedFrom":subQ73}),makeQuery(id+"F14.boolean.opBoolean","COPY",FACE,{"disambiguationData":[TD([makeQuery(id+"F6.opLoft","SWEPT_FACE",FACE,{"disambiguationData":[OSD([subQ32,subQ31,subQ30,subQ143,subQ140,subQ142])]})])],"derivedFrom":subQ73}),makeQuery(id+"F14.boolean.opBoolean","COPY",FACE,{"disambiguationData":[TD([makeQuery(id+"F6.opLoft","SWEPT_FACE",FACE,{"disambiguationData":[OSD([subQ62,subQ23,subQ22,subQ139,subQ138,subQ136])]})])],"derivedFrom":subQ73}),makeQuery(id+"F14.boolean.opBoolean","COPY",FACE,{"disambiguationData":[TD([makeQuery(id+"F6.opLoft","SWEPT_FACE",FACE,{"disambiguationData":[OSD([subQ28,subQ15,subQ14,subQ135,subQ132,subQ134])]})])],"derivedFrom":subQ73}),makeQuery(id+"F14.boolean.opBoolean","COPY",FACE,{"disambiguationData":[TD([makeQuery(id+"F6.opLoft","SWEPT_FACE",FACE,{"disambiguationData":[OSD([subQ20,subQ7,subQ6,subQ131,subQ128,subQ130])]})])],"derivedFrom":subQ73}),makeQuery(id+"F14.boolean.opBoolean","COPY",FACE,{"disambiguationData":[TD([makeQuery(id+"F6.opLoft","SWEPT_FACE",FACE,{"disambiguationData":[OSD([subQ12,subQ1,subQ0,subQ127,subQ126,subQ124])]})])],"derivedFrom":subQ73}),makeQuery(id+"F14.boolean.opBoolean","COPY",FACE,{"disambiguationData":[TD([makeQuery(id+"F6.opLoft","SWEPT_FACE",FACE,{"disambiguationData":[OSD([subQ36,subQ45,subQ44,subQ123,subQ122,subQ120])]})])],"derivedFrom":subQ73}),makeQuery(id+"F14.boolean.opBoolean","COPY",FACE,{"disambiguationData":[TD([makeQuery(id+"F6.opLoft","SWEPT_FACE",FACE,{"disambiguationData":[OSD([subQ56,subQ55,subQ54,subQ119,subQ118,subQ81])]})])],"derivedFrom":subQ73}),makeQuery(id+"F14.boolean.opBoolean","COPY",FACE,{"disambiguationData":[TD([makeQuery(id+"F6.opLoft","SWEPT_FACE",FACE,{"disambiguationData":[OSD([subQ68,subQ39,subQ38,subQ79,subQ78,subQ77])]})])],"derivedFrom":subQ73}),makeQuery(id+"F14.boolean.opBoolean","COPY",FACE,{"disambiguationData":[TD([makeQuery(id+"F4.opLoft","SWEPT_FACE",FACE,{"disambiguationData":[OSD([subQ49,subQ53,subQ52,subQ48,subQ51,subQ50])]})])],"derivedFrom":subQ73})]});}
            fillet(context, id + "F16", {"entities" : qUnion([Q0, Q1]), "radius" : 2 * mm, "tangentPropagation" : true, "allowEdgeOverflow" : false});
        }
        {
            var Q0;
            Q0=qCreatedBy(makeId("Front.planeOp"),FACE);
            var sketch = newSketch(context, id + "F17", { "sketchPlane" : qUnion([Q0])});
            skFitSpline(sketch, "E108", {"points": [v(0, 7.41) * mm, v(18.74, 20.95) * mm, v(30.07, 62.12) * mm, v(45.18, 89.18) * mm, v(59.13, 105.52) * mm, v(53.34, 112.41) * mm, v(43.2, 95.65) * mm, v(35.6, 86.08) * mm, v(30.25, 77.07) * mm, v(24.7, 57.17) * mm, v(19.9, 34.08) * mm, v(11.82, 18.1) * mm, v(0, 11.36) * mm], "startDerivative": vector(168.7, -54.25) * mm, "endDerivative": vector(-169.95, -0.84) * mm});
            skLineSegment(sketch, "E109", {"start": v(0, 11.36) * mm, "end": v(0, 7.41) * mm});
            skLineSegment(sketch, "E110", {"start": v(0, 7.41) * mm, "end": v(0, 112.41) * mm, "construction": true});
            skLineSegment(sketch, "E111", {"start": v(0, 112.41) * mm, "end": v(0, 91.77) * mm, "construction": true});
            skSolve(sketch);
        }
        {
            var Q0;
            Q0 = qSketchRegion(id + "F17", true);
            var Q1;
            Q1=sQuery(id+"F17.wireOp",EDGE,"E109");
            revolve(context, id + "F18", {"entities" : qUnion([Q0]), "axis" : qUnion([Q1]), "revolveType" : RevolveType.FULL});
        }
        {
            var Q0;
            {var subQ0=sQuery(id+"F5.wireOp",EDGE,"E51.trimOffspring");var subQ1=sQuery(id+"F5.wireOp",EDGE,"E44.8.2");var subQ2=sQuery(id+"F5.wireOp",EDGE,"E44.8.1");Q0=makeQuery(id+"F9.boolean.opBoolean","MERGE",EDGE,{"derivedFrom":[makeQuery(id+"F6.opLoft","MID_CAP_EDGE",EDGE,{"disambiguationData":[OSD([subQ2,subQ1,subQ0])],"capPos":0.0}),makeQuery(id+"F9.opLoft","MID_CAP_EDGE",EDGE,{"disambiguationData":[OSD([subQ2,subQ1,subQ0])],"capPos":1.0})]});}
            var Q1;
            {var subQ0=sQuery(id+"F5.wireOp",EDGE,"E50.trimOffspring");var subQ1=sQuery(id+"F5.wireOp",EDGE,"E44.7.2");var subQ2=sQuery(id+"F5.wireOp",EDGE,"E44.7.1");Q1=makeQuery(id+"F9.boolean.opBoolean","MERGE",EDGE,{"derivedFrom":[makeQuery(id+"F6.opLoft","MID_CAP_EDGE",EDGE,{"disambiguationData":[OSD([subQ2,subQ1,subQ0])],"capPos":0.0}),makeQuery(id+"F9.opLoft","MID_CAP_EDGE",EDGE,{"disambiguationData":[OSD([subQ2,subQ1,subQ0])],"capPos":1.0})]});}
            var Q2;
            {var subQ0=sQuery(id+"F5.wireOp",EDGE,"E49.trimOffspring");var subQ1=sQuery(id+"F5.wireOp",EDGE,"E44.6.2");var subQ2=sQuery(id+"F5.wireOp",EDGE,"E44.6.1");Q2=makeQuery(id+"F9.boolean.opBoolean","MERGE",EDGE,{"derivedFrom":[makeQuery(id+"F6.opLoft","MID_CAP_EDGE",EDGE,{"disambiguationData":[OSD([subQ2,subQ1,subQ0])],"capPos":0.0}),makeQuery(id+"F9.opLoft","MID_CAP_EDGE",EDGE,{"disambiguationData":[OSD([subQ2,subQ1,subQ0])],"capPos":1.0})]});}
            var Q3;
            {var subQ0=sQuery(id+"F3.wireOp",EDGE,"E28.trimOffspring");var subQ1=sQuery(id+"F3.wireOp",EDGE,"E23.6.2");var subQ2=sQuery(id+"F3.wireOp",EDGE,"E23.6.1");Q3=makeQuery(id+"F15.opBoolean","MERGE",EDGE,{"derivedFrom":[makeQuery(id+"F4.opLoft","MID_CAP_EDGE",EDGE,{"disambiguationData":[OSD([subQ2,subQ1,subQ0])],"capPos":0.0}),makeQuery(id+"F6.opLoft","MID_CAP_EDGE",EDGE,{"disambiguationData":[OSD([subQ2,subQ1,subQ0])],"capPos":1.0})]});}
            var Q4;
            {var subQ0=sQuery(id+"F3.wireOp",EDGE,"E29.trimOffspring");var subQ1=sQuery(id+"F3.wireOp",EDGE,"E23.7.2");var subQ2=sQuery(id+"F3.wireOp",EDGE,"E23.7.1");Q4=makeQuery(id+"F15.opBoolean","MERGE",EDGE,{"derivedFrom":[makeQuery(id+"F4.opLoft","MID_CAP_EDGE",EDGE,{"disambiguationData":[OSD([subQ2,subQ1,subQ0])],"capPos":0.0}),makeQuery(id+"F6.opLoft","MID_CAP_EDGE",EDGE,{"disambiguationData":[OSD([subQ2,subQ1,subQ0])],"capPos":1.0})]});}
            var Q5;
            {var subQ0=sQuery(id+"F3.wireOp",EDGE,"E30.trimOffspring");var subQ1=sQuery(id+"F3.wireOp",EDGE,"E23.8.2");var subQ2=sQuery(id+"F3.wireOp",EDGE,"E23.8.1");Q5=makeQuery(id+"F15.opBoolean","MERGE",EDGE,{"derivedFrom":[makeQuery(id+"F4.opLoft","MID_CAP_EDGE",EDGE,{"disambiguationData":[OSD([subQ2,subQ1,subQ0])],"capPos":0.0}),makeQuery(id+"F6.opLoft","MID_CAP_EDGE",EDGE,{"disambiguationData":[OSD([subQ2,subQ1,subQ0])],"capPos":1.0})]});}
            var Q6;
            {var subQ0=sQuery(id+"F5.wireOp",EDGE,"E59.trimOffspring");var subQ1=sQuery(id+"F5.wireOp",EDGE,"E44.5.2");var subQ2=sQuery(id+"F5.wireOp",EDGE,"E44.5.1");Q6=makeQuery(id+"F9.boolean.opBoolean","MERGE",EDGE,{"derivedFrom":[makeQuery(id+"F6.opLoft","MID_CAP_EDGE",EDGE,{"disambiguationData":[OSD([subQ2,subQ1,subQ0])],"capPos":0.0}),makeQuery(id+"F9.opLoft","MID_CAP_EDGE",EDGE,{"disambiguationData":[OSD([subQ2,subQ1,subQ0])],"capPos":1.0})]});}
            var Q7;
            {var subQ0=sQuery(id+"F3.wireOp",EDGE,"E38.trimOffspring");var subQ1=sQuery(id+"F3.wireOp",EDGE,"E23.5.2");var subQ2=sQuery(id+"F3.wireOp",EDGE,"E23.5.1");Q7=makeQuery(id+"F15.opBoolean","MERGE",EDGE,{"derivedFrom":[makeQuery(id+"F4.opLoft","MID_CAP_EDGE",EDGE,{"disambiguationData":[OSD([subQ2,subQ1,subQ0])],"capPos":0.0}),makeQuery(id+"F6.opLoft","MID_CAP_EDGE",EDGE,{"disambiguationData":[OSD([subQ2,subQ1,subQ0])],"capPos":1.0})]});}
            var Q8;
            {var subQ0=sQuery(id+"F3.wireOp",EDGE,"E37.trimOffspring");var subQ1=sQuery(id+"F3.wireOp",EDGE,"E23.4.2");var subQ2=sQuery(id+"F3.wireOp",EDGE,"E23.4.1");Q8=makeQuery(id+"F15.opBoolean","MERGE",EDGE,{"derivedFrom":[makeQuery(id+"F4.opLoft","MID_CAP_EDGE",EDGE,{"disambiguationData":[OSD([subQ2,subQ1,subQ0])],"capPos":0.0}),makeQuery(id+"F6.opLoft","MID_CAP_EDGE",EDGE,{"disambiguationData":[OSD([subQ2,subQ1,subQ0])],"capPos":1.0})]});}
            var Q9;
            {var subQ0=sQuery(id+"F5.wireOp",EDGE,"E58.trimOffspring");var subQ1=sQuery(id+"F5.wireOp",EDGE,"E44.4.2");var subQ2=sQuery(id+"F5.wireOp",EDGE,"E44.4.1");Q9=makeQuery(id+"F9.boolean.opBoolean","MERGE",EDGE,{"derivedFrom":[makeQuery(id+"F6.opLoft","MID_CAP_EDGE",EDGE,{"disambiguationData":[OSD([subQ2,subQ1,subQ0])],"capPos":0.0}),makeQuery(id+"F9.opLoft","MID_CAP_EDGE",EDGE,{"disambiguationData":[OSD([subQ2,subQ1,subQ0])],"capPos":1.0})]});}
            var Q10;
            {var subQ0=sQuery(id+"F5.wireOp",EDGE,"E56.trimOffspring");var subQ1=sQuery(id+"F5.wireOp",EDGE,"E44.3.2");var subQ2=sQuery(id+"F5.wireOp",EDGE,"E44.3.1");Q10=makeQuery(id+"F9.boolean.opBoolean","MERGE",EDGE,{"derivedFrom":[makeQuery(id+"F6.opLoft","MID_CAP_EDGE",EDGE,{"disambiguationData":[OSD([subQ2,subQ1,subQ0])],"capPos":0.0}),makeQuery(id+"F9.opLoft","MID_CAP_EDGE",EDGE,{"disambiguationData":[OSD([subQ2,subQ1,subQ0])],"capPos":1.0})]});}
            var Q11;
            {var subQ0=sQuery(id+"F3.wireOp",EDGE,"E35.trimOffspring");var subQ1=sQuery(id+"F3.wireOp",EDGE,"E23.3.2");var subQ2=sQuery(id+"F3.wireOp",EDGE,"E23.3.1");Q11=makeQuery(id+"F15.opBoolean","MERGE",EDGE,{"derivedFrom":[makeQuery(id+"F4.opLoft","MID_CAP_EDGE",EDGE,{"disambiguationData":[OSD([subQ2,subQ1,subQ0])],"capPos":0.0}),makeQuery(id+"F6.opLoft","MID_CAP_EDGE",EDGE,{"disambiguationData":[OSD([subQ2,subQ1,subQ0])],"capPos":1.0})]});}
            var Q12;
            {var subQ0=sQuery(id+"F3.wireOp",EDGE,"E32.trimOffspring");var subQ1=sQuery(id+"F3.wireOp",EDGE,"E23.2.2");var subQ2=sQuery(id+"F3.wireOp",EDGE,"E23.2.1");Q12=makeQuery(id+"F15.opBoolean","MERGE",EDGE,{"derivedFrom":[makeQuery(id+"F4.opLoft","MID_CAP_EDGE",EDGE,{"disambiguationData":[OSD([subQ2,subQ1,subQ0])],"capPos":0.0}),makeQuery(id+"F6.opLoft","MID_CAP_EDGE",EDGE,{"disambiguationData":[OSD([subQ2,subQ1,subQ0])],"capPos":1.0})]});}
            var Q13;
            {var subQ0=sQuery(id+"F5.wireOp",EDGE,"E53.trimOffspring");var subQ1=sQuery(id+"F5.wireOp",EDGE,"E44.2.2");var subQ2=sQuery(id+"F5.wireOp",EDGE,"E44.2.1");Q13=makeQuery(id+"F9.boolean.opBoolean","MERGE",EDGE,{"derivedFrom":[makeQuery(id+"F6.opLoft","MID_CAP_EDGE",EDGE,{"disambiguationData":[OSD([subQ2,subQ1,subQ0])],"capPos":0.0}),makeQuery(id+"F9.opLoft","MID_CAP_EDGE",EDGE,{"disambiguationData":[OSD([subQ2,subQ1,subQ0])],"capPos":1.0})]});}
            var Q14;
            {var subQ0=sQuery(id+"F3.wireOp",EDGE,"E31.trimOffspring");var subQ1=sQuery(id+"F3.wireOp",EDGE,"E23.1.2");var subQ2=sQuery(id+"F3.wireOp",EDGE,"E23.1.1");Q14=makeQuery(id+"F15.opBoolean","MERGE",EDGE,{"derivedFrom":[makeQuery(id+"F4.opLoft","MID_CAP_EDGE",EDGE,{"disambiguationData":[OSD([subQ2,subQ1,subQ0])],"capPos":0.0}),makeQuery(id+"F6.opLoft","MID_CAP_EDGE",EDGE,{"disambiguationData":[OSD([subQ2,subQ1,subQ0])],"capPos":1.0})]});}
            var Q15;
            {var subQ0=sQuery(id+"F5.wireOp",EDGE,"E52.trimOffspring");var subQ1=sQuery(id+"F5.wireOp",EDGE,"E44.1.2");var subQ2=sQuery(id+"F5.wireOp",EDGE,"E44.1.1");Q15=makeQuery(id+"F9.boolean.opBoolean","MERGE",EDGE,{"derivedFrom":[makeQuery(id+"F6.opLoft","MID_CAP_EDGE",EDGE,{"disambiguationData":[OSD([subQ2,subQ1,subQ0])],"capPos":0.0}),makeQuery(id+"F9.opLoft","MID_CAP_EDGE",EDGE,{"disambiguationData":[OSD([subQ2,subQ1,subQ0])],"capPos":1.0})]});}
            var Q16;
            {var subQ0=sQuery(id+"F3.wireOp",EDGE,"E27.trimOffspring");var subQ1=sQuery(id+"F3.wireOp",EDGE,"E22");var subQ2=sQuery(id+"F3.wireOp",EDGE,"E21");Q16=makeQuery(id+"F15.opBoolean","MERGE",EDGE,{"derivedFrom":[makeQuery(id+"F4.opLoft","MID_CAP_EDGE",EDGE,{"disambiguationData":[OSD([subQ2,subQ1,subQ0])],"capPos":0.0}),makeQuery(id+"F6.opLoft","MID_CAP_EDGE",EDGE,{"disambiguationData":[OSD([subQ2,subQ1,subQ0])],"capPos":1.0})]});}
            var Q17;
            {var subQ0=sQuery(id+"F5.wireOp",EDGE,"E48.trimOffspring");var subQ1=sQuery(id+"F5.wireOp",EDGE,"E43");var subQ2=sQuery(id+"F5.wireOp",EDGE,"E42");Q17=makeQuery(id+"F9.boolean.opBoolean","MERGE",EDGE,{"derivedFrom":[makeQuery(id+"F6.opLoft","MID_CAP_EDGE",EDGE,{"disambiguationData":[OSD([subQ2,subQ1,subQ0])],"capPos":0.0}),makeQuery(id+"F9.opLoft","MID_CAP_EDGE",EDGE,{"disambiguationData":[OSD([subQ2,subQ1,subQ0])],"capPos":1.0})]});}
            var Q18;
            {var subQ0=sQuery(id+"F8.wireOp",EDGE,"E77.trimOffspring");var subQ1=sQuery(id+"F8.wireOp",EDGE,"E65.3.2");var subQ2=sQuery(id+"F8.wireOp",EDGE,"E65.3.1");Q18=makeQuery(id+"F15.opBoolean","MERGE",EDGE,{"derivedFrom":[makeQuery(id+"F9.opLoft","MID_CAP_EDGE",EDGE,{"disambiguationData":[OSD([subQ2,subQ1,subQ0])],"capPos":0.0}),makeQuery(id+"F12.opLoft","MID_CAP_EDGE",EDGE,{"disambiguationData":[OSD([subQ2,subQ1,subQ0])],"capPos":1.0})]});}
            var Q19;
            {var subQ0=sQuery(id+"F8.wireOp",EDGE,"E79.trimOffspring");var subQ1=sQuery(id+"F8.wireOp",EDGE,"E65.4.2");var subQ2=sQuery(id+"F8.wireOp",EDGE,"E65.4.1");Q19=makeQuery(id+"F15.opBoolean","MERGE",EDGE,{"derivedFrom":[makeQuery(id+"F9.opLoft","MID_CAP_EDGE",EDGE,{"disambiguationData":[OSD([subQ2,subQ1,subQ0])],"capPos":0.0}),makeQuery(id+"F12.opLoft","MID_CAP_EDGE",EDGE,{"disambiguationData":[OSD([subQ2,subQ1,subQ0])],"capPos":1.0})]});}
            var Q20;
            {var subQ0=sQuery(id+"F8.wireOp",EDGE,"E80.trimOffspring");var subQ1=sQuery(id+"F8.wireOp",EDGE,"E65.5.2");var subQ2=sQuery(id+"F8.wireOp",EDGE,"E65.5.1");Q20=makeQuery(id+"F15.opBoolean","MERGE",EDGE,{"derivedFrom":[makeQuery(id+"F9.opLoft","MID_CAP_EDGE",EDGE,{"disambiguationData":[OSD([subQ2,subQ1,subQ0])],"capPos":0.0}),makeQuery(id+"F12.opLoft","MID_CAP_EDGE",EDGE,{"disambiguationData":[OSD([subQ2,subQ1,subQ0])],"capPos":1.0})]});}
            var Q21;
            {var subQ0=sQuery(id+"F8.wireOp",EDGE,"E70.trimOffspring");var subQ1=sQuery(id+"F8.wireOp",EDGE,"E65.6.2");var subQ2=sQuery(id+"F8.wireOp",EDGE,"E65.6.1");Q21=makeQuery(id+"F15.opBoolean","MERGE",EDGE,{"derivedFrom":[makeQuery(id+"F9.opLoft","MID_CAP_EDGE",EDGE,{"disambiguationData":[OSD([subQ2,subQ1,subQ0])],"capPos":0.0}),makeQuery(id+"F12.opLoft","MID_CAP_EDGE",EDGE,{"disambiguationData":[OSD([subQ2,subQ1,subQ0])],"capPos":1.0})]});}
            var Q22;
            {var subQ0=sQuery(id+"F8.wireOp",EDGE,"E71.trimOffspring");var subQ1=sQuery(id+"F8.wireOp",EDGE,"E65.7.2");var subQ2=sQuery(id+"F8.wireOp",EDGE,"E65.7.1");Q22=makeQuery(id+"F15.opBoolean","MERGE",EDGE,{"derivedFrom":[makeQuery(id+"F9.opLoft","MID_CAP_EDGE",EDGE,{"disambiguationData":[OSD([subQ2,subQ1,subQ0])],"capPos":0.0}),makeQuery(id+"F12.opLoft","MID_CAP_EDGE",EDGE,{"disambiguationData":[OSD([subQ2,subQ1,subQ0])],"capPos":1.0})]});}
            var Q23;
            {var subQ0=sQuery(id+"F8.wireOp",EDGE,"E72.trimOffspring");var subQ1=sQuery(id+"F8.wireOp",EDGE,"E65.8.2");var subQ2=sQuery(id+"F8.wireOp",EDGE,"E65.8.1");Q23=makeQuery(id+"F15.opBoolean","MERGE",EDGE,{"derivedFrom":[makeQuery(id+"F9.opLoft","MID_CAP_EDGE",EDGE,{"disambiguationData":[OSD([subQ2,subQ1,subQ0])],"capPos":0.0}),makeQuery(id+"F12.opLoft","MID_CAP_EDGE",EDGE,{"disambiguationData":[OSD([subQ2,subQ1,subQ0])],"capPos":1.0})]});}
            var Q24;
            {var subQ0=sQuery(id+"F8.wireOp",EDGE,"E69.trimOffspring");var subQ1=sQuery(id+"F8.wireOp",EDGE,"E64");var subQ2=sQuery(id+"F8.wireOp",EDGE,"E63");Q24=makeQuery(id+"F15.opBoolean","MERGE",EDGE,{"derivedFrom":[makeQuery(id+"F9.opLoft","MID_CAP_EDGE",EDGE,{"disambiguationData":[OSD([subQ2,subQ1,subQ0])],"capPos":0.0}),makeQuery(id+"F12.opLoft","MID_CAP_EDGE",EDGE,{"disambiguationData":[OSD([subQ2,subQ1,subQ0])],"capPos":1.0})]});}
            var Q25;
            {var subQ0=sQuery(id+"F8.wireOp",EDGE,"E73.trimOffspring");var subQ1=sQuery(id+"F8.wireOp",EDGE,"E65.1.2");var subQ2=sQuery(id+"F8.wireOp",EDGE,"E65.1.1");Q25=makeQuery(id+"F15.opBoolean","MERGE",EDGE,{"derivedFrom":[makeQuery(id+"F9.opLoft","MID_CAP_EDGE",EDGE,{"disambiguationData":[OSD([subQ2,subQ1,subQ0])],"capPos":0.0}),makeQuery(id+"F12.opLoft","MID_CAP_EDGE",EDGE,{"disambiguationData":[OSD([subQ2,subQ1,subQ0])],"capPos":1.0})]});}
            var Q26;
            {var subQ0=sQuery(id+"F8.wireOp",EDGE,"E74.trimOffspring");var subQ1=sQuery(id+"F8.wireOp",EDGE,"E65.2.2");var subQ2=sQuery(id+"F8.wireOp",EDGE,"E65.2.1");Q26=makeQuery(id+"F15.opBoolean","MERGE",EDGE,{"derivedFrom":[makeQuery(id+"F9.opLoft","MID_CAP_EDGE",EDGE,{"disambiguationData":[OSD([subQ2,subQ1,subQ0])],"capPos":0.0}),makeQuery(id+"F12.opLoft","MID_CAP_EDGE",EDGE,{"disambiguationData":[OSD([subQ2,subQ1,subQ0])],"capPos":1.0})]});}
            fillet(context, id + "F19", {"entities" : qUnion([Q0, Q1, Q2, Q3, Q4, Q5, Q6, Q7, Q8, Q9, Q10, Q11, Q12, Q13, Q14, Q15, Q16, Q17, Q18, Q19, Q20, Q21, Q22, Q23, Q24, Q25, Q26]), "radius" : 1 * mm, "tangentPropagation" : true, "allowEdgeOverflow" : false});
        }
    });
